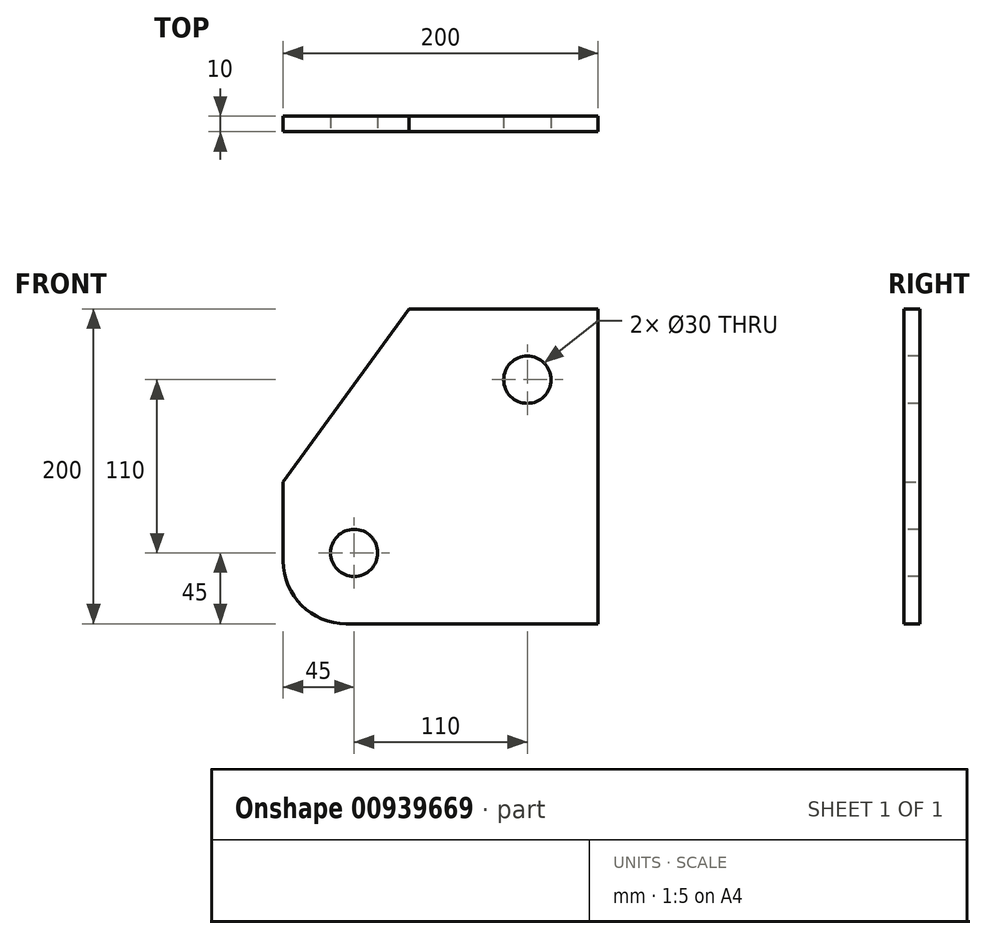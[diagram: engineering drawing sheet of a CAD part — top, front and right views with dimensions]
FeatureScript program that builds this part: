
annotation { "Feature Type Name" : "Feature", "Feature Type Description" : "" }
export const myFeature = defineFeature(function(context is Context, id is Id, definition is map)
    precondition{}
    {
        {
            var Q0;
            Q0=qCreatedBy(makeId("Front.planeOp"),FACE);
            var sketch = newSketch(context, id + "F0", { "sketchPlane" : qUnion([Q0])});
            skLineSegment(sketch, "E0.bottom", {"start": v(100, -100) * mm, "end": v(-100, -100) * mm});
            skLineSegment(sketch, "E0.top", {"start": v(100, 100) * mm, "end": v(-100, 100) * mm});
            skLineSegment(sketch, "E0.left", {"start": v(100, -100) * mm, "end": v(100, 100) * mm});
            skLineSegment(sketch, "E0.right", {"start": v(-100, -100) * mm, "end": v(-100, 100) * mm});
            skPoint(sketch, "E0.middle", {"position": v(0, 0) * mm});
            skSolve(sketch);
        }
        {
            var Q0;
            Q0 = qSketchRegion(id + "F0", true);
            extrude(context, id + "F1", {"entities" : qUnion([Q0]), "oppositeDirection" : true, "depth" : 10 * mm, "offsetDistance" : 25 * mm});
        }
        {
            var Q0;
            Q0=makeQuery(id+"F1.opExtrude","CAP_FACE",FACE,{"disambiguationData":[OSD([sQuery(id+"F0.wireOp",EDGE,"E0.bottom"),sQuery(id+"F0.wireOp",EDGE,"E0.top"),sQuery(id+"F0.wireOp",EDGE,"E0.left"),sQuery(id+"F0.wireOp",EDGE,"E0.right")])],"isStart":true});
            var sketch = newSketch(context, id + "F2", { "sketchPlane" : qUnion([Q0])});
            skSolve(sketch);
        }
        {
            var Q0;
            Q0=makeQuery(id+"F2.imprint","IMPRINT",FACE,{"disambiguationData":[TD([[makeQuery(id+"F2.imprint","IMPRINT",EDGE,{"derivedFrom":makeQuery(id+"F1.opExtrude","CAP_EDGE",EDGE,{"disambiguationData":[OSD([sQuery(id+"F0.wireOp",EDGE,"E0.bottom")])],"isStart":true})}),-1.0]])]});
            var sketch = newSketch(context, id + "F3", { "sketchPlane" : qUnion([Q0])});
            skCircle(sketch, "E1", {"center": v(-55, -55) * mm, "radius": 15 * mm});
            skCircle(sketch, "E2", {"center": v(55, 55) * mm, "radius": 15 * mm});
            skSolve(sketch);
        }
        {
            var Q0;
            Q0 = qSketchRegion(id + "F3", true);
            extrude(context, id + "F4", {"entities" : qUnion([Q0]), "operationType" : NewBodyOperationType.REMOVE, "endBound" : BoundingType.THROUGH_ALL, "oppositeDirection" : true, "depth" : 25 * mm, "offsetDistance" : 25 * mm});
        }
        {
            var Q0;
            Q0=makeQuery(id+"F1.opExtrude","SWEPT_EDGE",EDGE,{"disambiguationData":[OSD([sQuery(id+"F0.wireOp",EDGE,"E0.bottom"),sQuery(id+"F0.wireOp",EDGE,"E0.right")])]});
            fillet(context, id + "F5", {"entities" : qUnion([Q0]), "radius" : 40 * mm, "tangentPropagation" : true, "allowEdgeOverflow" : false});
        }
        {
            var Q0;
            Q0=makeQuery(id+"F1.opExtrude","SWEPT_EDGE",EDGE,{"disambiguationData":[OSD([sQuery(id+"F0.wireOp",EDGE,"E0.top"),sQuery(id+"F0.wireOp",EDGE,"E0.right")])]});
            chamfer(context, id + "F6", {"entities" : qUnion([Q0]), "chamferType" : ChamferType.TWO_OFFSETS, "width1" : 80 * mm, "oppositeDirection" : false, "width2" : 110 * mm, "tangentPropagation" : true});
        }
    });
